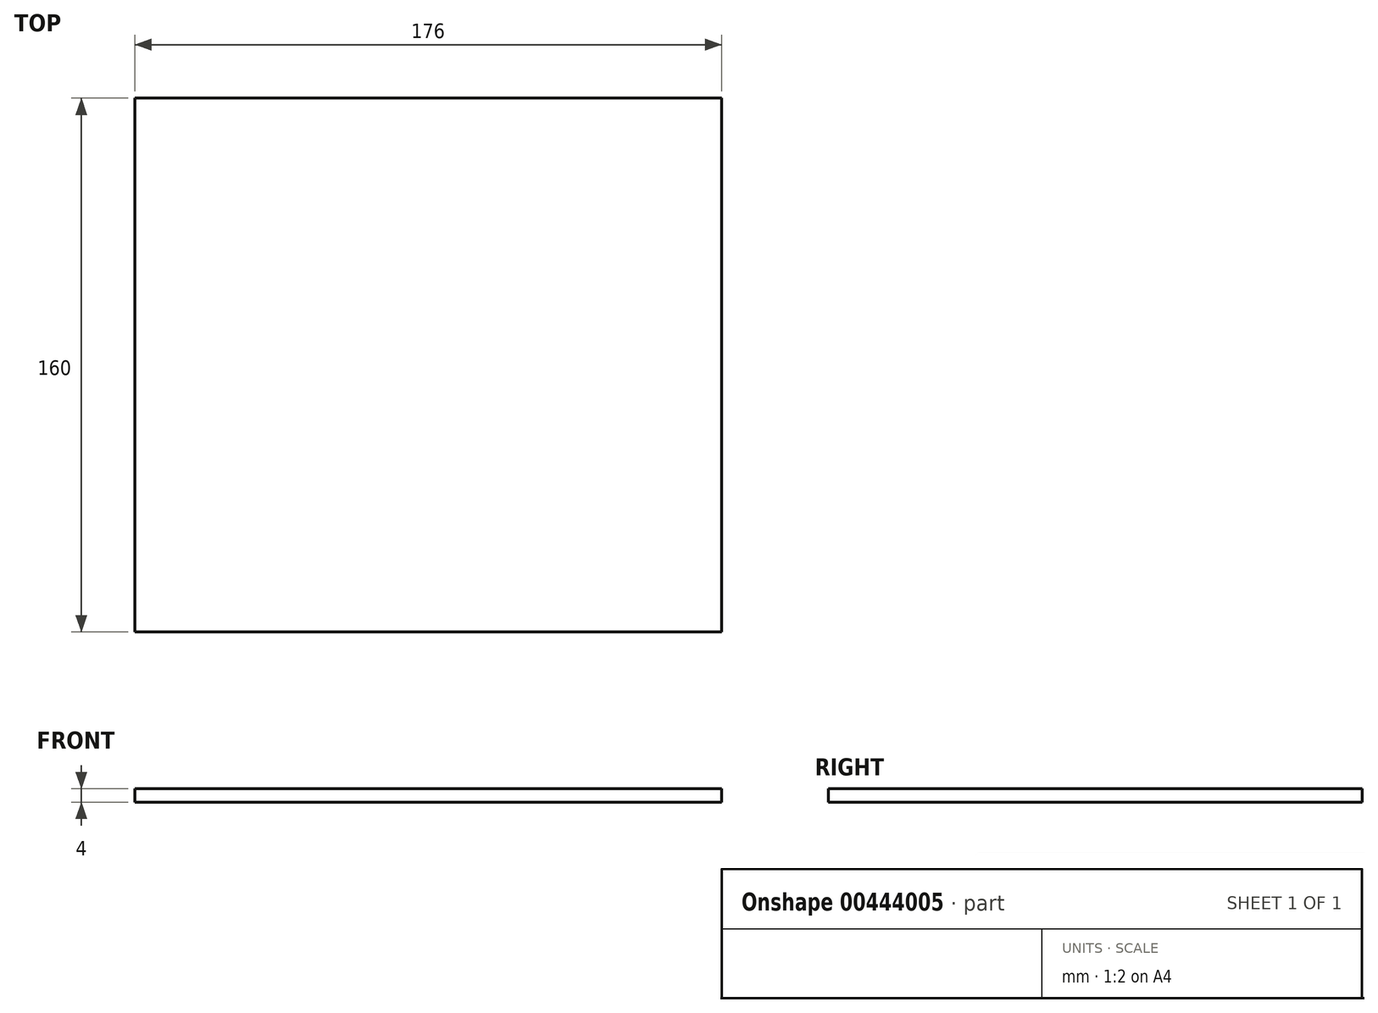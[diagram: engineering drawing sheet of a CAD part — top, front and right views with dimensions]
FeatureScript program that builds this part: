
annotation { "Feature Type Name" : "Feature", "Feature Type Description" : "" }
export const myFeature = defineFeature(function(context is Context, id is Id, definition is map)
    precondition{}
    {
        {
            var Q0;
            Q0=qCreatedBy(makeId("Top.planeOp"),FACE);
            var sketch = newSketch(context, id + "F0", { "sketchPlane" : qUnion([Q0])});
            skLineSegment(sketch, "E0.bottom", {"start": v(-61.33, -48.38) * mm, "end": v(114.67, -48.38) * mm});
            skLineSegment(sketch, "E0.top", {"start": v(-61.33, 111.62) * mm, "end": v(114.67, 111.62) * mm});
            skLineSegment(sketch, "E0.left", {"start": v(-61.33, -48.38) * mm, "end": v(-61.33, 111.62) * mm});
            skLineSegment(sketch, "E0.right", {"start": v(114.67, -48.38) * mm, "end": v(114.67, 111.62) * mm});
            skSolve(sketch);
        }
        {
            var Q0;
            Q0=makeQuery(id+"F0.imprint","IMPRINT",FACE,{"disambiguationData":[TD([[makeQuery(id+"F0.imprint","IMPRINT",EDGE,{"derivedFrom":sQuery(id+"F0.wireOp",EDGE,"E0.bottom")}),1.0]])]});
            extrude(context, id + "F1", {"entities" : qUnion([Q0]), "depth" : 4 * mm});
        }
    });
